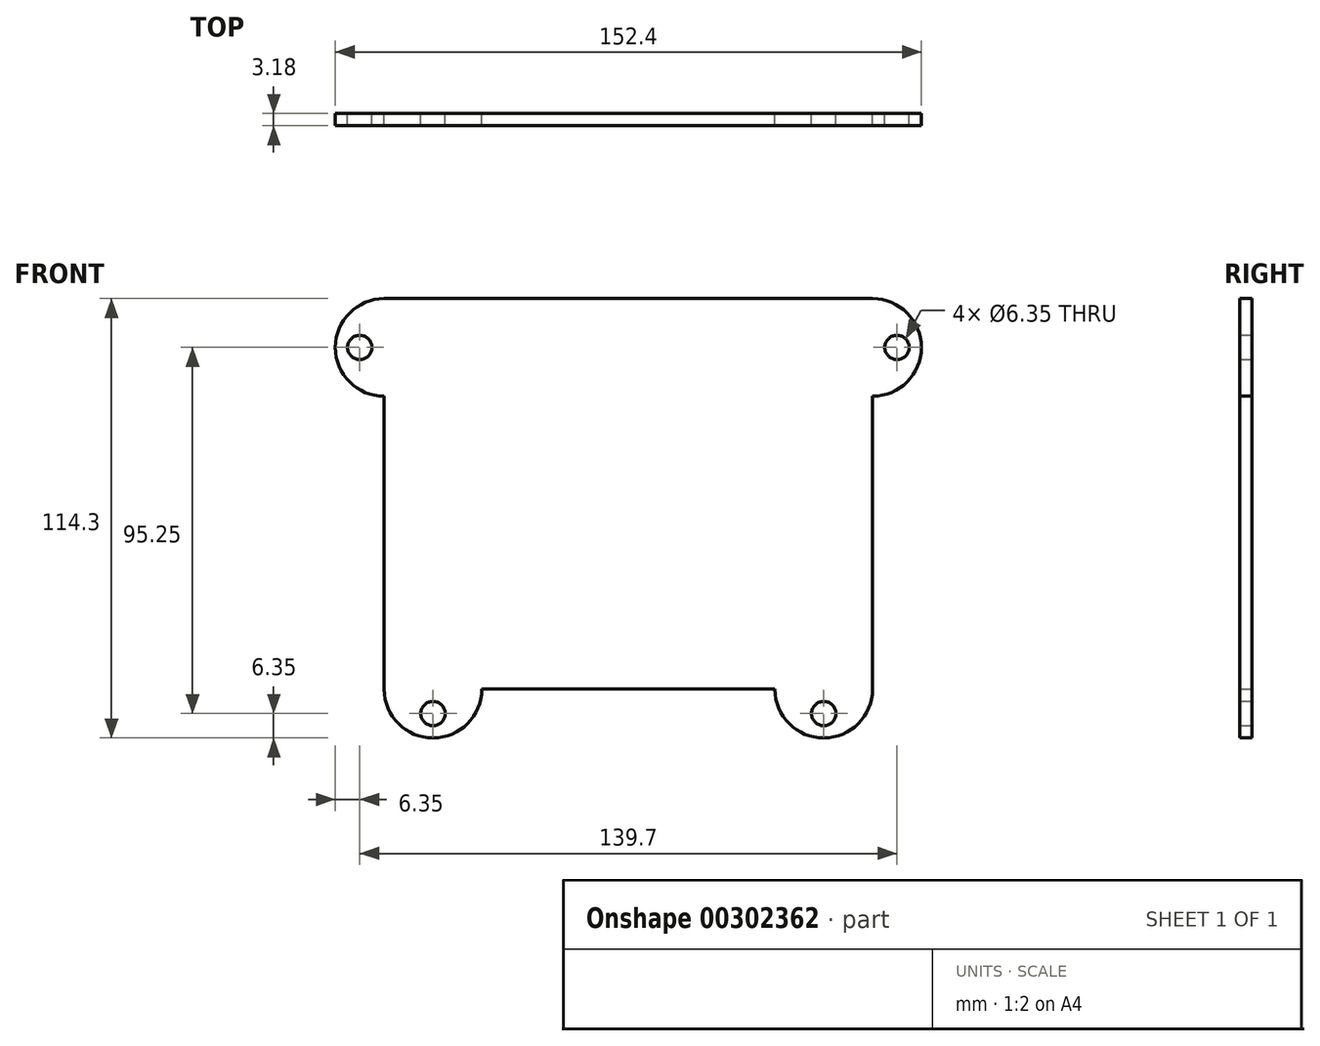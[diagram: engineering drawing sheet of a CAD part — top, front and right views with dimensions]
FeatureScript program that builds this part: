
annotation { "Feature Type Name" : "Feature", "Feature Type Description" : "" }
export const myFeature = defineFeature(function(context is Context, id is Id, definition is map)
    precondition{}
    {
        {
            var Q0;
            Q0=qCreatedBy(makeId("Front.planeOp"),FACE);
            var sketch = newSketch(context, id + "F0", { "sketchPlane" : qUnion([Q0])});
            skLineSegment(sketch, "E0.bottom", {"start": v(-63.5, 50.8) * mm, "end": v(63.5, 50.8) * mm});
            skLineSegment(sketch, "E0.top", {"start": v(-63.5, -50.8) * mm, "end": v(63.5, -50.8) * mm});
            skLineSegment(sketch, "E0.left", {"start": v(-63.5, 50.8) * mm, "end": v(-63.5, -50.8) * mm});
            skLineSegment(sketch, "E0.right", {"start": v(63.5, 50.8) * mm, "end": v(63.5, -50.8) * mm});
            skArc(sketch, "E1", {"start": v(-63.5, 50.8) * mm, "mid": v(-76.2, 38.1) * mm, "end": v(-63.5, 25.4) * mm});
            skArc(sketch, "E2", {"start": v(63.5, 25.4) * mm, "mid": v(76.2, 38.1) * mm, "end": v(63.5, 50.8) * mm});
            skArc(sketch, "E3", {"start": v(-63.5, -50.8) * mm, "mid": v(-50.8, -63.5) * mm, "end": v(-38.1, -50.8) * mm});
            skArc(sketch, "E4", {"start": v(38.1, -50.8) * mm, "mid": v(50.8, -63.5) * mm, "end": v(63.5, -50.8) * mm});
            skCircle(sketch, "E5", {"center": v(-69.85, 38.1) * mm, "radius": 3.18 * mm});
            skLineSegment(sketch, "E6", {"start": v(-63.5, 38.1) * mm, "end": v(-76.2, 38.1) * mm, "construction": true});
            skLineSegment(sketch, "E7", {"start": v(0, 72.65) * mm, "end": v(0, -71.53) * mm, "construction": true});
            skLineSegment(sketch, "E8", {"start": v(-50.8, -50.8) * mm, "end": v(-50.8, -63.5) * mm, "construction": true});
            skCircle(sketch, "E9", {"center": v(-50.8, -57.15) * mm, "radius": 3.18 * mm});
            skCircle(sketch, "E10.MirrorC", {"center": v(50.8, -57.15) * mm, "radius": 3.18 * mm});
            skCircle(sketch, "E11.MirrorC", {"center": v(69.85, 38.1) * mm, "radius": 3.18 * mm});
            skSolve(sketch);
        }
        {
            var Q0;
            {var subQ0=sQuery(id+"F0.wireOp",EDGE,"E1");Q0=makeQuery(id+"F0.imprint","IMPRINT",FACE,{"disambiguationData":[TD([[makeQuery(id+"F0.imprint","IMPRINT",EDGE,{"derivedFrom":subQ0}),1.0]])]});}
            var Q1;
            {var subQ9=sQuery(id+"F0.wireOp",EDGE,"E0.bottom");Q1=makeQuery(id+"F0.imprint","IMPRINT",FACE,{"disambiguationData":[TD([[makeQuery(id+"F0.imprint","IMPRINT",EDGE,{"derivedFrom":subQ9}),-1.0]])]});}
            var Q2;
            {var subQ0=sQuery(id+"F0.wireOp",EDGE,"E2");Q2=makeQuery(id+"F0.imprint","IMPRINT",FACE,{"disambiguationData":[TD([[makeQuery(id+"F0.imprint","IMPRINT",EDGE,{"derivedFrom":subQ0}),1.0]])]});}
            var Q3;
            {var subQ0=sQuery(id+"F0.wireOp",EDGE,"E4");Q3=makeQuery(id+"F0.imprint","IMPRINT",FACE,{"disambiguationData":[TD([[makeQuery(id+"F0.imprint","IMPRINT",EDGE,{"derivedFrom":subQ0}),1.0]])]});}
            var Q4;
            {var subQ0=sQuery(id+"F0.wireOp",EDGE,"E3");Q4=makeQuery(id+"F0.imprint","IMPRINT",FACE,{"disambiguationData":[TD([[makeQuery(id+"F0.imprint","IMPRINT",EDGE,{"derivedFrom":subQ0}),1.0]])]});}
            extrude(context, id + "F1", {"entities" : qUnion([Q0, Q1, Q2, Q3, Q4]), "depth" : 3.17 * mm});
        }
    });
